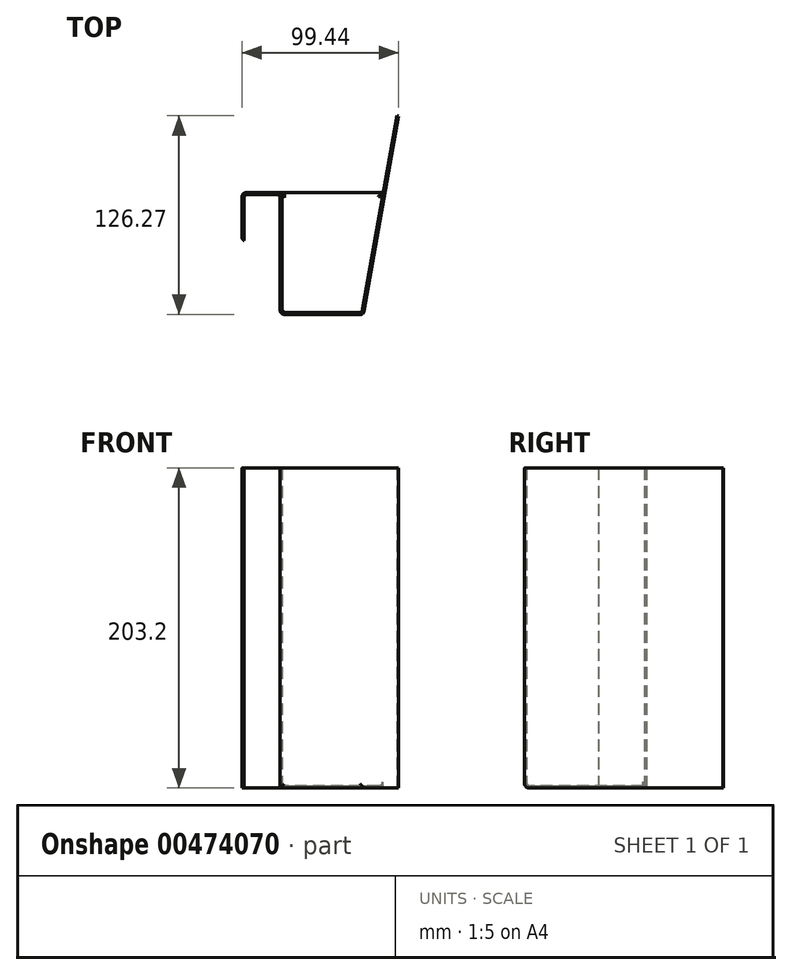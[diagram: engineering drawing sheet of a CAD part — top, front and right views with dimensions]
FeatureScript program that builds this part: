
annotation { "Feature Type Name" : "Feature", "Feature Type Description" : "" }
export const myFeature = defineFeature(function(context is Context, id is Id, definition is map)
    precondition{}
    {
        {
            var Q0;
            Q0=qCreatedBy(makeId("Top.planeOp"),FACE);
            var sketch = newSketch(context, id + "F0", { "sketchPlane" : qUnion([Q0])});
            skLineSegment(sketch, "E0", {"start": v(-77.17, 0) * mm, "end": v(-77.17, 30.54) * mm});
            skLineSegment(sketch, "E1", {"start": v(-77.17, 30.54) * mm, "end": v(-51.77, 30.54) * mm});
            skLineSegment(sketch, "E2", {"start": v(-51.77, 30.54) * mm, "end": v(-51.77, -45.66) * mm});
            skLineSegment(sketch, "E3", {"start": v(-51.77, -45.66) * mm, "end": v(-0.97, -45.66) * mm});
            skLineSegment(sketch, "E4", {"start": v(-0.97, -45.66) * mm, "end": v(21.09, 79.4) * mm});
            skLineSegment(sketch, "E5.0", {"start": v(0.04, -46.86) * mm, "end": v(22.27, 79.2) * mm});
            skLineSegment(sketch, "E5.1", {"start": v(-75.97, 0) * mm, "end": v(-75.97, 29.34) * mm});
            skLineSegment(sketch, "E5.2", {"start": v(-75.97, 29.34) * mm, "end": v(-52.97, 29.34) * mm});
            skLineSegment(sketch, "E5.3", {"start": v(-52.97, 29.34) * mm, "end": v(-52.97, -46.86) * mm});
            skLineSegment(sketch, "E5.4", {"start": v(-52.97, -46.86) * mm, "end": v(0.04, -46.86) * mm});
            skLineSegment(sketch, "E6", {"start": v(-51.77, 30.54) * mm, "end": v(12.47, 30.54) * mm});
            skLineSegment(sketch, "E7", {"start": v(-77.17, 0) * mm, "end": v(-75.97, 0) * mm});
            skLineSegment(sketch, "E8", {"start": v(21.09, 79.4) * mm, "end": v(22.27, 79.2) * mm});
            skSolve(sketch);
        }
        {
            var Q0;
            Q0=makeQuery(id+"F0.imprint","IMPRINT",FACE,{"disambiguationData":[TD([[makeQuery(id+"F0.imprint","IMPRINT",EDGE,{"derivedFrom":sQuery(id+"F0.wireOp",EDGE,"E0")}),-1.0]])]});
            extrude(context, id + "F1", {"entities" : qUnion([Q0]), "depth" : 203.2 * mm, "offsetDistance" : 25.4 * mm});
        }
        {
            var Q0;
            Q0=makeQuery(id+"F0.imprint","IMPRINT",FACE,{"disambiguationData":[TD([[makeQuery(id+"F0.imprint","IMPRINT",EDGE,{"derivedFrom":sQuery(id+"F0.wireOp",EDGE,"E2")}),1.0]])]});
            extrude(context, id + "F2", {"entities" : qUnion([Q0]), "operationType" : NewBodyOperationType.ADD, "depth" : 1.2 * mm, "offsetDistance" : 25.4 * mm});
        }
        {
            var Q0;
            Q0=makeQuery(id+"F2.opExtrude","CAP_EDGE",EDGE,{"disambiguationData":[OSD([sQuery(id+"F0.wireOp",EDGE,"E4")])],"isStart":false});
            var Q1;
            Q1=makeQuery(id+"F1.opExtrude","SWEPT_EDGE",EDGE,{"disambiguationData":[OSD([sQuery(id+"F0.wireOp",EDGE,"E3"),sQuery(id+"F0.wireOp",EDGE,"E4")])]});
            var Q2;
            Q2=makeQuery(id+"F2.opExtrude","CAP_EDGE",EDGE,{"disambiguationData":[OSD([sQuery(id+"F0.wireOp",EDGE,"E3")])],"isStart":false});
            var Q3;
            Q3=makeQuery(id+"F2.opExtrude","CAP_EDGE",EDGE,{"disambiguationData":[OSD([sQuery(id+"F0.wireOp",EDGE,"E2")])],"isStart":false});
            var Q4;
            Q4=makeQuery(id+"F1.opExtrude","SWEPT_EDGE",EDGE,{"disambiguationData":[OSD([sQuery(id+"F0.wireOp",EDGE,"E2"),sQuery(id+"F0.wireOp",EDGE,"E3")])]});
            fillet(context, id + "F3", {"entities" : qUnion([Q0, Q1, Q2, Q3, Q4]), "radius" : 2.54 * mm, "tangentPropagation" : true, "allowEdgeOverflow" : false});
        }
        {
            var Q0;
            Q0=makeQuery(id+"F1.opExtrude","SWEPT_EDGE",EDGE,{"disambiguationData":[OSD([sQuery(id+"F0.wireOp",EDGE,"E5.3"),sQuery(id+"F0.wireOp",EDGE,"E5.4")])]});
            var Q1;
            Q1=makeQuery(id+"F1.opExtrude","SWEPT_EDGE",EDGE,{"disambiguationData":[OSD([sQuery(id+"F0.wireOp",EDGE,"E5.2"),sQuery(id+"F0.wireOp",EDGE,"E5.3")])]});
            var Q2;
            Q2=makeQuery(id+"F1.opExtrude","SWEPT_EDGE",EDGE,{"disambiguationData":[OSD([sQuery(id+"F0.wireOp",EDGE,"E5.1"),sQuery(id+"F0.wireOp",EDGE,"E5.2")])]});
            var Q3;
            Q3=makeQuery(id+"F1.opExtrude","SWEPT_EDGE",EDGE,{"disambiguationData":[OSD([sQuery(id+"F0.wireOp",EDGE,"E5.0"),sQuery(id+"F0.wireOp",EDGE,"E5.4")])]});
            var Q4;
            Q4=makeQuery(id+"F1.opExtrude","CAP_EDGE",EDGE,{"disambiguationData":[OSD([sQuery(id+"F0.wireOp",EDGE,"E5.4")])],"isStart":true});
            fillet(context, id + "F4", {"entities" : qUnion([Q0, Q1, Q2, Q3, Q4]), "radius" : 2.54 * mm, "tangentPropagation" : true, "allowEdgeOverflow" : false});
        }
        {
            var Q0;
            Q0=makeQuery(id+"F1.opExtrude","SWEPT_EDGE",EDGE,{"disambiguationData":[OSD([sQuery(id+"F0.wireOp",EDGE,"E1"),sQuery(id+"F0.wireOp",EDGE,"E2"),sQuery(id+"F0.wireOp",EDGE,"E6")])]});
            var Q1;
            Q1=makeQuery(id+"F1.opExtrude","SWEPT_EDGE",EDGE,{"disambiguationData":[OSD([sQuery(id+"F0.wireOp",EDGE,"E0"),sQuery(id+"F0.wireOp",EDGE,"E1")])]});
            var Q2;
            Q2=makeQuery(id+"F1.opExtrude","SWEPT_EDGE",EDGE,{"disambiguationData":[OSD([sQuery(id+"F0.wireOp",EDGE,"E0"),sQuery(id+"F0.wireOp",EDGE,"E7")])]});
            fillet(context, id + "F5", {"entities" : qUnion([Q0, Q1, Q2]), "radius" : 2.54 * mm, "tangentPropagation" : true, "allowEdgeOverflow" : false});
        }
    });
